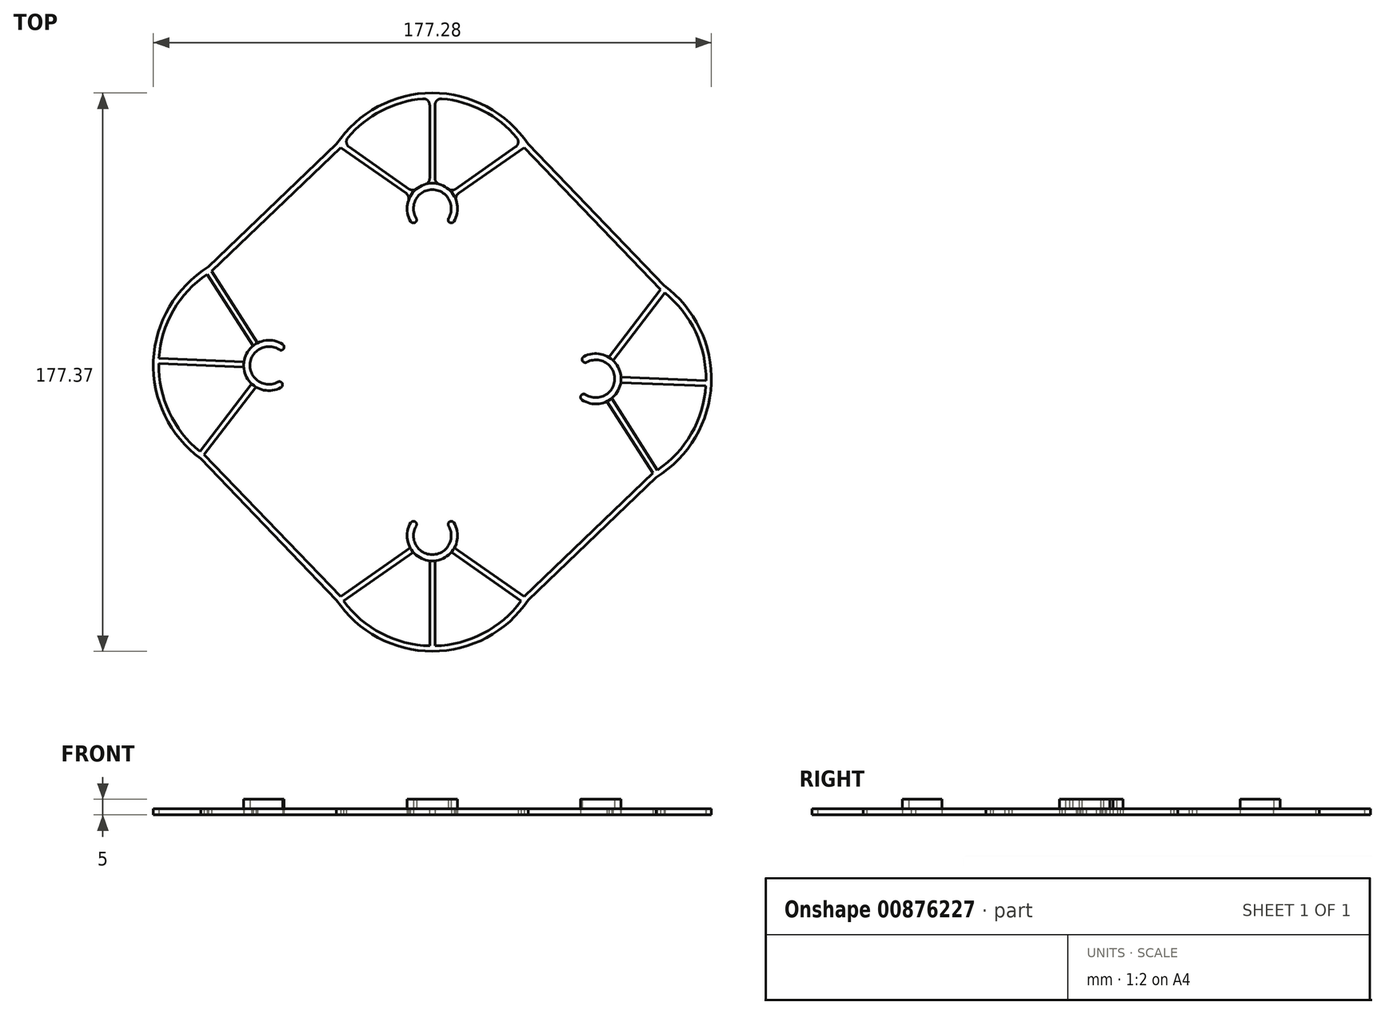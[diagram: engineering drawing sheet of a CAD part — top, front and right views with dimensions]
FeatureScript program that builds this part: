
annotation { "Feature Type Name" : "Feature", "Feature Type Description" : "" }
export const myFeature = defineFeature(function(context is Context, id is Id, definition is map)
    precondition{}
    {
        {
            var Q0;
            Q0=qCreatedBy(makeId("Top.planeOp"),FACE);
            var sketch = newSketch(context, id + "F0", { "sketchPlane" : qUnion([Q0])});
            skArc(sketch, "E0", {"start": v(5, -3.32) * mm, "mid": v(0, 6) * mm, "end": v(-5, -3.32) * mm});
            skArc(sketch, "E1", {"start": v(-7, 3.87) * mm, "mid": v(-7.85, -1.56) * mm, "end": v(-5, -6.24) * mm});
            skLineSegment(sketch, "E2", {"start": v(-7, 3.87) * mm, "end": v(-29.15, 19.37) * mm});
            skArc(sketch, "E3", {"start": v(28.17, 20.77) * mm, "mid": v(16.16, 31.05) * mm, "end": v(0.85, 34.99) * mm});
            skLineSegment(sketch, "E4", {"start": v(-6.03, 5.26) * mm, "end": v(-28.17, 20.77) * mm});
            skLineSegment(sketch, "E5", {"start": v(0, 0) * mm, "end": v(-28.67, 20.08) * mm, "construction": true});
            skLineSegment(sketch, "E6", {"start": v(0, 0) * mm, "end": v(0, 35) * mm, "construction": true});
            skLineSegment(sketch, "E7.MirrorCS", {"start": v(6.03, 5.26) * mm, "end": v(28.17, 20.77) * mm});
            skLineSegment(sketch, "E8.MirrorCS", {"start": v(7, 3.87) * mm, "end": v(29.15, 19.37) * mm});
            skLineSegment(sketch, "E9", {"start": v(-0.85, 7.95) * mm, "end": v(-0.85, 34.99) * mm});
            skLineSegment(sketch, "E10", {"start": v(0.85, 34.99) * mm, "end": v(0.85, 7.95) * mm});
            skArc(sketch, "E11", {"start": v(30.49, 20.43) * mm, "mid": v(0, 36.7) * mm, "end": v(-30.49, 20.43) * mm});
            skArc(sketch, "E12.trimOffspring", {"start": v(-0.85, 7.95) * mm, "mid": v(-3.7, 7.1) * mm, "end": v(-6.03, 5.26) * mm});
            skArc(sketch, "E13.trimOffspring", {"start": v(6.03, 5.26) * mm, "mid": v(3.7, 7.1) * mm, "end": v(0.85, 7.95) * mm});
            skArc(sketch, "E14.trimOffspring", {"start": v(-0.85, 34.99) * mm, "mid": v(-16.16, 31.05) * mm, "end": v(-28.17, 20.77) * mm});
            skPoint(sketch, "E15.middle", {"position": v(0, -9.2) * mm});
            skPoint(sketch, "E15.bottom.start.orphan", {"position": v(-4, -0.06) * mm});
            skPoint(sketch, "E16.orphan", {"position": v(4, 0.05) * mm});
            skArc(sketch, "E17.trimOffspring", {"start": v(5, -6.24) * mm, "mid": v(7.85, -1.56) * mm, "end": v(7, 3.87) * mm});
            skPoint(sketch, "E15.top.end.orphan", {"position": v(4, -18.32) * mm});
            skPoint(sketch, "E15.top.start.orphan", {"position": v(-4, -18.43) * mm});
            skLineSegment(sketch, "E18", {"start": v(0, 0) * mm, "end": v(51.94, -54.1) * mm, "construction": true});
            skLineSegment(sketch, "E19", {"start": v(51.94, -54.1) * mm, "end": v(0, -103.97) * mm, "construction": true});
            skLineSegment(sketch, "E20", {"start": v(0, -103.97) * mm, "end": v(-51.94, -49.86) * mm, "construction": true});
            skLineSegment(sketch, "E21", {"start": v(-51.94, -49.86) * mm, "end": v(0, 0) * mm, "construction": true});
            skLineSegment(sketch, "E22", {"start": v(0, 0) * mm, "end": v(0, -103.97) * mm, "construction": true});
            skLineSegment(sketch, "E23", {"start": v(51.94, -54.1) * mm, "end": v(-51.94, -49.86) * mm, "construction": true});
            skLineSegment(sketch, "E24", {"start": v(0, -51.98) * mm, "end": v(54.15, 0) * mm, "construction": true});
            skLineSegment(sketch, "E25.MirrorCS", {"start": v(48.42, -58.96) * mm, "end": v(45.5, -58.85) * mm});
            skLineSegment(sketch, "E26.MirrorCS", {"start": v(48.83, -48.97) * mm, "end": v(45.9, -48.85) * mm});
            skArc(sketch, "E27.MirrorCS", {"start": v(57.44, -48.3) * mm, "mid": v(59.18, -50.7) * mm, "end": v(59.92, -53.58) * mm});
            skArc(sketch, "E28.MirrorCS", {"start": v(59.85, -55.28) * mm, "mid": v(58.88, -58.08) * mm, "end": v(56.95, -60.34) * mm});
            skLineSegment(sketch, "E29.MirrorCS", {"start": v(55.52, -61.26) * mm, "end": v(70.1, -84.02) * mm});
            skLineSegment(sketch, "E30.MirrorCS", {"start": v(57.44, -48.3) * mm, "end": v(73.84, -26.8) * mm});
            skArc(sketch, "E31.MirrorCS", {"start": v(55.52, -61.26) * mm, "mid": v(50.07, -61.88) * mm, "end": v(45.5, -58.85) * mm});
            skPoint(sketch, "E32.MirrorP", {"position": v(51.71, -58.1) * mm});
            skLineSegment(sketch, "E33.MirrorCS", {"start": v(56.09, -47.26) * mm, "end": v(72.49, -25.77) * mm});
            skLineSegment(sketch, "E34.MirrorCS", {"start": v(56.95, -60.34) * mm, "end": v(71.54, -83.1) * mm});
            skArc(sketch, "E35.MirrorCS", {"start": v(73.6, -24.47) * mm, "mid": v(88.6, -55.6) * mm, "end": v(71.1, -85.4) * mm});
            skArc(sketch, "E36.MirrorCS", {"start": v(73.84, -26.8) * mm, "mid": v(83.62, -39.22) * mm, "end": v(86.94, -54.68) * mm});
            skLineSegment(sketch, "E37.MirrorCS", {"start": v(59.85, -55.28) * mm, "end": v(86.87, -56.38) * mm});
            skLineSegment(sketch, "E38.MirrorCS", {"start": v(86.94, -54.68) * mm, "end": v(59.92, -53.58) * mm});
            skArc(sketch, "E39.MirrorCS", {"start": v(48.83, -48.97) * mm, "mid": v(57.93, -54.35) * mm, "end": v(48.42, -58.96) * mm});
            skPoint(sketch, "E40.MirrorP", {"position": v(52.15, -50.1) * mm});
            skArc(sketch, "E41.MirrorCS", {"start": v(45.9, -48.85) * mm, "mid": v(50.7, -46.2) * mm, "end": v(56.09, -47.26) * mm});
            skArc(sketch, "E42.MirrorCS", {"start": v(86.87, -56.38) * mm, "mid": v(82.3, -71.52) * mm, "end": v(71.54, -83.1) * mm});
            skLineSegment(sketch, "E43", {"start": v(0, -51.98) * mm, "end": v(-83.37, 34.86) * mm, "construction": true});
            skArc(sketch, "E44.MirrorCS", {"start": v(-45.9, -55.11) * mm, "mid": v(-50.7, -57.77) * mm, "end": v(-56.09, -56.7) * mm});
            skLineSegment(sketch, "E45.MirrorCS", {"start": v(-48.83, -55) * mm, "end": v(-45.9, -55.11) * mm});
            skArc(sketch, "E46.MirrorCS", {"start": v(-57.44, -55.67) * mm, "mid": v(-59.18, -53.26) * mm, "end": v(-59.92, -50.39) * mm});
            skLineSegment(sketch, "E47.MirrorCS", {"start": v(-48.42, -45) * mm, "end": v(-45.5, -45.12) * mm});
            skArc(sketch, "E48.MirrorCS", {"start": v(-73.6, -79.5) * mm, "mid": v(-88.6, -48.36) * mm, "end": v(-71.1, -18.57) * mm});
            skArc(sketch, "E49.MirrorCS", {"start": v(-59.85, -48.69) * mm, "mid": v(-58.88, -45.88) * mm, "end": v(-56.95, -43.62) * mm});
            skArc(sketch, "E50.MirrorCS", {"start": v(-73.84, -77.17) * mm, "mid": v(-83.62, -64.74) * mm, "end": v(-86.94, -49.28) * mm});
            skPoint(sketch, "E51.MirrorP", {"position": v(-52.15, -53.86) * mm});
            skArc(sketch, "E52.MirrorCS", {"start": v(-86.87, -47.59) * mm, "mid": v(-82.3, -32.45) * mm, "end": v(-71.54, -20.86) * mm});
            skLineSegment(sketch, "E53.MirrorCS", {"start": v(-59.85, -48.69) * mm, "end": v(-86.87, -47.59) * mm});
            skPoint(sketch, "E54.MirrorP", {"position": v(-42.76, -50.24) * mm});
            skArc(sketch, "E55.MirrorCS", {"start": v(-48.83, -55) * mm, "mid": v(-57.93, -49.62) * mm, "end": v(-48.42, -45) * mm});
            skLineSegment(sketch, "E56.MirrorCS", {"start": v(-56.95, -43.62) * mm, "end": v(-71.54, -20.86) * mm});
            skArc(sketch, "E57.MirrorCS", {"start": v(-55.52, -42.7) * mm, "mid": v(-50.07, -42.08) * mm, "end": v(-45.5, -45.12) * mm});
            skLineSegment(sketch, "E58.MirrorCS", {"start": v(-56.09, -56.7) * mm, "end": v(-72.49, -78.2) * mm});
            skLineSegment(sketch, "E59.MirrorCS", {"start": v(-55.52, -42.7) * mm, "end": v(-70.1, -19.95) * mm});
            skPoint(sketch, "E60.MirrorP", {"position": v(-51.71, -45.87) * mm});
            skLineSegment(sketch, "E61.MirrorCS", {"start": v(-57.44, -55.67) * mm, "end": v(-73.84, -77.17) * mm});
            skLineSegment(sketch, "E62.MirrorCS", {"start": v(-86.94, -49.28) * mm, "end": v(-59.92, -50.39) * mm});
            skLineSegment(sketch, "E63.MirrorCS", {"start": v(-5, -100.65) * mm, "end": v(-5, -97.72) * mm});
            skArc(sketch, "E64.MirrorCS", {"start": v(0.85, -111.92) * mm, "mid": v(3.7, -111.06) * mm, "end": v(6.03, -109.23) * mm});
            skArc(sketch, "E65.MirrorCS", {"start": v(-6.03, -109.23) * mm, "mid": v(-3.7, -111.06) * mm, "end": v(-0.85, -111.92) * mm});
            skLineSegment(sketch, "E66.MirrorCS", {"start": v(5, -100.65) * mm, "end": v(5, -97.72) * mm});
            skLineSegment(sketch, "E67.MirrorCS", {"start": v(-6.03, -109.23) * mm, "end": v(-28.17, -124.73) * mm});
            skArc(sketch, "E68.MirrorCS", {"start": v(-30.49, -124.4) * mm, "mid": v(0, -140.67) * mm, "end": v(30.49, -124.4) * mm});
            skArc(sketch, "E69.MirrorCS", {"start": v(-5, -97.72) * mm, "mid": v(-7.85, -102.41) * mm, "end": v(-7, -107.83) * mm});
            skArc(sketch, "E70.MirrorCS", {"start": v(-5, -100.65) * mm, "mid": v(0, -109.97) * mm, "end": v(5, -100.65) * mm});
            skArc(sketch, "E71.MirrorCS", {"start": v(-28.17, -124.73) * mm, "mid": v(-16.16, -135.01) * mm, "end": v(-0.85, -138.96) * mm});
            skPoint(sketch, "E72.MirrorP", {"position": v(-4, -104.01) * mm});
            skLineSegment(sketch, "E73.MirrorCS", {"start": v(-7, -107.83) * mm, "end": v(-29.15, -123.34) * mm});
            skLineSegment(sketch, "E74.MirrorCS", {"start": v(0.85, -111.92) * mm, "end": v(0.85, -138.96) * mm});
            skArc(sketch, "E75.MirrorCS", {"start": v(7, -107.83) * mm, "mid": v(7.85, -102.41) * mm, "end": v(5, -97.72) * mm});
            skPoint(sketch, "E76.MirrorP", {"position": v(4, -103.9) * mm});
            skLineSegment(sketch, "E77.MirrorCS", {"start": v(-0.85, -138.96) * mm, "end": v(-0.85, -111.92) * mm});
            skLineSegment(sketch, "E78.MirrorCS", {"start": v(7, -107.83) * mm, "end": v(29.15, -123.34) * mm});
            skLineSegment(sketch, "E79.MirrorCS", {"start": v(6.03, -109.23) * mm, "end": v(28.17, -124.73) * mm});
            skArc(sketch, "E80.MirrorCS", {"start": v(0.85, -138.96) * mm, "mid": v(16.16, -135.01) * mm, "end": v(28.17, -124.73) * mm});
            skLineSegment(sketch, "E81", {"start": v(73.6, -24.47) * mm, "end": v(30.49, 20.43) * mm});
            skLineSegment(sketch, "E82", {"start": v(72.49, -25.77) * mm, "end": v(29.15, 19.37) * mm});
            skLineSegment(sketch, "E83", {"start": v(71.1, -85.4) * mm, "end": v(30.49, -124.4) * mm});
            skLineSegment(sketch, "E84", {"start": v(70.1, -84.02) * mm, "end": v(29.15, -123.34) * mm});
            skLineSegment(sketch, "E85", {"start": v(-30.49, -124.4) * mm, "end": v(-73.6, -79.5) * mm});
            skLineSegment(sketch, "E86", {"start": v(-29.15, -123.34) * mm, "end": v(-72.49, -78.2) * mm});
            skLineSegment(sketch, "E87", {"start": v(-71.1, -18.57) * mm, "end": v(-30.49, 20.43) * mm});
            skLineSegment(sketch, "E88", {"start": v(-29.15, 19.37) * mm, "end": v(-70.1, -19.95) * mm});
            skLineSegment(sketch, "E89", {"start": v(-5, -3.32) * mm, "end": v(-5, -6.24) * mm});
            skLineSegment(sketch, "E90", {"start": v(5, -3.32) * mm, "end": v(5, -6.24) * mm});
            skSolve(sketch);
        }
        {
            var Q0;
            Q0=qSketchRegion(id+"F0",true);
            extrude(context, id + "F1", {"entities" : qUnion([Q0]), "depth" : 2 * mm});
        }
        {
            var Q0;
            Q0=makeQuery(id+"F1.opExtrude","SWEPT_EDGE",EDGE,{"disambiguationData":[OSD([sQuery(id+"F0.wireOp",EDGE,"E0"),sQuery(id+"F0.wireOp",EDGE,"E89")])]});
            var Q1;
            Q1=makeQuery(id+"F1.opExtrude","SWEPT_EDGE",EDGE,{"disambiguationData":[OSD([sQuery(id+"F0.wireOp",EDGE,"E1"),sQuery(id+"F0.wireOp",EDGE,"E89")])]});
            var Q2;
            Q2=makeQuery(id+"F1.opExtrude","SWEPT_EDGE",EDGE,{"disambiguationData":[OSD([sQuery(id+"F0.wireOp",EDGE,"E0"),sQuery(id+"F0.wireOp",EDGE,"E90")])]});
            var Q3;
            Q3=makeQuery(id+"F1.opExtrude","SWEPT_EDGE",EDGE,{"disambiguationData":[OSD([sQuery(id+"F0.wireOp",EDGE,"E17.trimOffspring"),sQuery(id+"F0.wireOp",EDGE,"E90")])]});
            var Q4;
            Q4=makeQuery(id+"F1.opExtrude","SWEPT_EDGE",EDGE,{"disambiguationData":[OSD([sQuery(id+"F0.wireOp",EDGE,"E26.MirrorCS"),sQuery(id+"F0.wireOp",EDGE,"E39.MirrorCS")])]});
            var Q5;
            Q5=makeQuery(id+"F1.opExtrude","SWEPT_EDGE",EDGE,{"disambiguationData":[OSD([sQuery(id+"F0.wireOp",EDGE,"E26.MirrorCS"),sQuery(id+"F0.wireOp",EDGE,"E41.MirrorCS")])]});
            var Q6;
            Q6=makeQuery(id+"F1.opExtrude","SWEPT_EDGE",EDGE,{"disambiguationData":[OSD([sQuery(id+"F0.wireOp",EDGE,"E25.MirrorCS"),sQuery(id+"F0.wireOp",EDGE,"E39.MirrorCS")])]});
            var Q7;
            Q7=makeQuery(id+"F1.opExtrude","SWEPT_EDGE",EDGE,{"disambiguationData":[OSD([sQuery(id+"F0.wireOp",EDGE,"E25.MirrorCS"),sQuery(id+"F0.wireOp",EDGE,"E31.MirrorCS")])]});
            var Q8;
            Q8=makeQuery(id+"F1.opExtrude","SWEPT_EDGE",EDGE,{"disambiguationData":[OSD([sQuery(id+"F0.wireOp",EDGE,"E66.MirrorCS"),sQuery(id+"F0.wireOp",EDGE,"E70.MirrorCS")])]});
            var Q9;
            Q9=makeQuery(id+"F1.opExtrude","SWEPT_EDGE",EDGE,{"disambiguationData":[OSD([sQuery(id+"F0.wireOp",EDGE,"E66.MirrorCS"),sQuery(id+"F0.wireOp",EDGE,"E75.MirrorCS")])]});
            var Q10;
            Q10=makeQuery(id+"F1.opExtrude","SWEPT_EDGE",EDGE,{"disambiguationData":[OSD([sQuery(id+"F0.wireOp",EDGE,"E63.MirrorCS"),sQuery(id+"F0.wireOp",EDGE,"E69.MirrorCS")])]});
            var Q11;
            Q11=makeQuery(id+"F1.opExtrude","SWEPT_EDGE",EDGE,{"disambiguationData":[OSD([sQuery(id+"F0.wireOp",EDGE,"E63.MirrorCS"),sQuery(id+"F0.wireOp",EDGE,"E70.MirrorCS")])]});
            var Q12;
            Q12=makeQuery(id+"F1.opExtrude","SWEPT_EDGE",EDGE,{"disambiguationData":[OSD([sQuery(id+"F0.wireOp",EDGE,"E45.MirrorCS"),sQuery(id+"F0.wireOp",EDGE,"E55.MirrorCS")])]});
            var Q13;
            Q13=makeQuery(id+"F1.opExtrude","SWEPT_EDGE",EDGE,{"disambiguationData":[OSD([sQuery(id+"F0.wireOp",EDGE,"E44.MirrorCS"),sQuery(id+"F0.wireOp",EDGE,"E45.MirrorCS")])]});
            var Q14;
            Q14=makeQuery(id+"F1.opExtrude","SWEPT_EDGE",EDGE,{"disambiguationData":[OSD([sQuery(id+"F0.wireOp",EDGE,"E47.MirrorCS"),sQuery(id+"F0.wireOp",EDGE,"E55.MirrorCS")])]});
            var Q15;
            Q15=makeQuery(id+"F1.opExtrude","SWEPT_EDGE",EDGE,{"disambiguationData":[OSD([sQuery(id+"F0.wireOp",EDGE,"E47.MirrorCS"),sQuery(id+"F0.wireOp",EDGE,"E57.MirrorCS")])]});
            fillet(context, id + "F2", {"entities" : qUnion([Q0, Q1, Q2, Q3, Q4, Q5, Q6, Q7, Q8, Q9, Q10, Q11, Q12, Q13, Q14, Q15]), "radius" : 1 * mm, "tangentPropagation" : true, "allowEdgeOverflow" : false});
        }
        {
            var Q0;
            Q0=makeQuery(id+"F1.opExtrude","SWEPT_EDGE",EDGE,{"disambiguationData":[OSD([sQuery(id+"F0.wireOp",EDGE,"E7.MirrorCS"),sQuery(id+"F0.wireOp",EDGE,"E13.trimOffspring")])]});
            var Q1;
            Q1=makeQuery(id+"F1.opExtrude","SWEPT_EDGE",EDGE,{"disambiguationData":[OSD([sQuery(id+"F0.wireOp",EDGE,"E10"),sQuery(id+"F0.wireOp",EDGE,"E13.trimOffspring")])]});
            var Q2;
            Q2=makeQuery(id+"F1.opExtrude","SWEPT_EDGE",EDGE,{"disambiguationData":[OSD([sQuery(id+"F0.wireOp",EDGE,"E8.MirrorCS"),sQuery(id+"F0.wireOp",EDGE,"E17.trimOffspring")])]});
            var Q3;
            Q3=makeQuery(id+"F1.opExtrude","SWEPT_EDGE",EDGE,{"disambiguationData":[OSD([sQuery(id+"F0.wireOp",EDGE,"E9"),sQuery(id+"F0.wireOp",EDGE,"E12.trimOffspring")])]});
            var Q4;
            Q4=makeQuery(id+"F1.opExtrude","SWEPT_EDGE",EDGE,{"disambiguationData":[OSD([sQuery(id+"F0.wireOp",EDGE,"E1"),sQuery(id+"F0.wireOp",EDGE,"E2")])]});
            var Q5;
            Q5=makeQuery(id+"F1.opExtrude","SWEPT_EDGE",EDGE,{"disambiguationData":[OSD([sQuery(id+"F0.wireOp",EDGE,"E4"),sQuery(id+"F0.wireOp",EDGE,"E12.trimOffspring")])]});
            var Q6;
            Q6=makeQuery(id+"F1.opExtrude","SWEPT_EDGE",EDGE,{"disambiguationData":[OSD([sQuery(id+"F0.wireOp",EDGE,"E3"),sQuery(id+"F0.wireOp",EDGE,"E7.MirrorCS")])]});
            var Q7;
            Q7=makeQuery(id+"F1.opExtrude","SWEPT_EDGE",EDGE,{"disambiguationData":[OSD([sQuery(id+"F0.wireOp",EDGE,"E4"),sQuery(id+"F0.wireOp",EDGE,"E14.trimOffspring")])]});
            var Q8;
            Q8=makeQuery(id+"F1.opExtrude","SWEPT_EDGE",EDGE,{"disambiguationData":[OSD([sQuery(id+"F0.wireOp",EDGE,"E9"),sQuery(id+"F0.wireOp",EDGE,"E14.trimOffspring")])]});
            var Q9;
            Q9=makeQuery(id+"F1.opExtrude","SWEPT_EDGE",EDGE,{"disambiguationData":[OSD([sQuery(id+"F0.wireOp",EDGE,"E3"),sQuery(id+"F0.wireOp",EDGE,"E10")])]});
            fillet(context, id + "F3", {"entities" : qUnion([Q0, Q1, Q2, Q3, Q4, Q5, Q6, Q7, Q8, Q9]), "radius" : 2 * mm, "tangentPropagation" : true, "allowEdgeOverflow" : false});
        }
        {
            var Q0;
            Q0=makeQuery(id+"F1.opExtrude","CAP_FACE",FACE,{"disambiguationData":[OSD([sQuery(id+"F0.wireOp",EDGE,"E0"),sQuery(id+"F0.wireOp",EDGE,"E1"),sQuery(id+"F0.wireOp",EDGE,"E2"),sQuery(id+"F0.wireOp",EDGE,"E3"),sQuery(id+"F0.wireOp",EDGE,"E4"),sQuery(id+"F0.wireOp",EDGE,"E7.MirrorCS"),sQuery(id+"F0.wireOp",EDGE,"E8.MirrorCS"),sQuery(id+"F0.wireOp",EDGE,"E9"),sQuery(id+"F0.wireOp",EDGE,"E10"),sQuery(id+"F0.wireOp",EDGE,"E11"),sQuery(id+"F0.wireOp",EDGE,"E12.trimOffspring"),sQuery(id+"F0.wireOp",EDGE,"E13.trimOffspring"),sQuery(id+"F0.wireOp",EDGE,"E14.trimOffspring"),sQuery(id+"F0.wireOp",EDGE,"E15.left"),sQuery(id+"F0.wireOp",EDGE,"E15.right"),sQuery(id+"F0.wireOp",EDGE,"E17.trimOffspring"),sQuery(id+"F0.wireOp",EDGE,"E25.MirrorCS"),sQuery(id+"F0.wireOp",EDGE,"E26.MirrorCS"),sQuery(id+"F0.wireOp",EDGE,"E27.MirrorCS"),sQuery(id+"F0.wireOp",EDGE,"E28.MirrorCS"),sQuery(id+"F0.wireOp",EDGE,"E29.MirrorCS"),sQuery(id+"F0.wireOp",EDGE,"E30.MirrorCS"),sQuery(id+"F0.wireOp",EDGE,"E31.MirrorCS"),sQuery(id+"F0.wireOp",EDGE,"E33.MirrorCS"),sQuery(id+"F0.wireOp",EDGE,"E34.MirrorCS"),sQuery(id+"F0.wireOp",EDGE,"E35.MirrorCS"),sQuery(id+"F0.wireOp",EDGE,"E36.MirrorCS"),sQuery(id+"F0.wireOp",EDGE,"E37.MirrorCS"),sQuery(id+"F0.wireOp",EDGE,"E38.MirrorCS"),sQuery(id+"F0.wireOp",EDGE,"E39.MirrorCS"),sQuery(id+"F0.wireOp",EDGE,"E41.MirrorCS"),sQuery(id+"F0.wireOp",EDGE,"E42.MirrorCS"),sQuery(id+"F0.wireOp",EDGE,"E44.MirrorCS"),sQuery(id+"F0.wireOp",EDGE,"E45.MirrorCS"),sQuery(id+"F0.wireOp",EDGE,"E46.MirrorCS"),sQuery(id+"F0.wireOp",EDGE,"E47.MirrorCS"),sQuery(id+"F0.wireOp",EDGE,"E48.MirrorCS"),sQuery(id+"F0.wireOp",EDGE,"E49.MirrorCS"),sQuery(id+"F0.wireOp",EDGE,"E50.MirrorCS"),sQuery(id+"F0.wireOp",EDGE,"E52.MirrorCS"),sQuery(id+"F0.wireOp",EDGE,"E53.MirrorCS"),sQuery(id+"F0.wireOp",EDGE,"E55.MirrorCS"),sQuery(id+"F0.wireOp",EDGE,"E56.MirrorCS"),sQuery(id+"F0.wireOp",EDGE,"E57.MirrorCS"),sQuery(id+"F0.wireOp",EDGE,"E58.MirrorCS"),sQuery(id+"F0.wireOp",EDGE,"E59.MirrorCS"),sQuery(id+"F0.wireOp",EDGE,"E61.MirrorCS"),sQuery(id+"F0.wireOp",EDGE,"E62.MirrorCS"),sQuery(id+"F0.wireOp",EDGE,"E63.MirrorCS"),sQuery(id+"F0.wireOp",EDGE,"E64.MirrorCS"),sQuery(id+"F0.wireOp",EDGE,"E65.MirrorCS"),sQuery(id+"F0.wireOp",EDGE,"E66.MirrorCS"),sQuery(id+"F0.wireOp",EDGE,"E67.MirrorCS"),sQuery(id+"F0.wireOp",EDGE,"E68.MirrorCS"),sQuery(id+"F0.wireOp",EDGE,"E69.MirrorCS"),sQuery(id+"F0.wireOp",EDGE,"E70.MirrorCS"),sQuery(id+"F0.wireOp",EDGE,"E71.MirrorCS"),sQuery(id+"F0.wireOp",EDGE,"E73.MirrorCS"),sQuery(id+"F0.wireOp",EDGE,"E74.MirrorCS"),sQuery(id+"F0.wireOp",EDGE,"E75.MirrorCS"),sQuery(id+"F0.wireOp",EDGE,"E77.MirrorCS"),sQuery(id+"F0.wireOp",EDGE,"E78.MirrorCS"),sQuery(id+"F0.wireOp",EDGE,"E79.MirrorCS"),sQuery(id+"F0.wireOp",EDGE,"E80.MirrorCS"),sQuery(id+"F0.wireOp",EDGE,"E81"),sQuery(id+"F0.wireOp",EDGE,"E82"),sQuery(id+"F0.wireOp",EDGE,"E83"),sQuery(id+"F0.wireOp",EDGE,"E84"),sQuery(id+"F0.wireOp",EDGE,"E85"),sQuery(id+"F0.wireOp",EDGE,"E86"),sQuery(id+"F0.wireOp",EDGE,"E87"),sQuery(id+"F0.wireOp",EDGE,"E88")])],"isStart":false});
            var sketch = newSketch(context, id + "F4", { "sketchPlane" : qUnion([Q0])});
            skLineSegment(sketch, "E91.0", {"start": v(73.6, -24.47) * mm, "end": v(30.49, 20.43) * mm});
            skArc(sketch, "E92.0", {"start": v(73.6, -24.47) * mm, "mid": v(88.6, -55.6) * mm, "end": v(71.1, -85.4) * mm});
            skLineSegment(sketch, "E93.0", {"start": v(71.1, -85.4) * mm, "end": v(30.49, -124.4) * mm});
            skArc(sketch, "E94.0", {"start": v(-30.49, -124.4) * mm, "mid": v(0, -140.67) * mm, "end": v(30.49, -124.4) * mm});
            skLineSegment(sketch, "E95.0", {"start": v(-30.49, -124.4) * mm, "end": v(-73.6, -79.5) * mm});
            skArc(sketch, "E96.0", {"start": v(-73.6, -79.5) * mm, "mid": v(-88.6, -48.36) * mm, "end": v(-71.1, -18.57) * mm});
            skLineSegment(sketch, "E97.0", {"start": v(-71.1, -18.57) * mm, "end": v(-30.49, 20.43) * mm});
            skArc(sketch, "E98.0", {"start": v(30.49, 20.43) * mm, "mid": v(0, 36.7) * mm, "end": v(-30.49, 20.43) * mm});
            skArc(sketch, "E99.0", {"start": v(72.7, -25.5) * mm, "mid": v(87.26, -55.56) * mm, "end": v(70.28, -84.33) * mm});
            skLineSegment(sketch, "E99.1", {"start": v(70.28, -84.33) * mm, "end": v(29.45, -123.52) * mm});
            skLineSegment(sketch, "E99.2", {"start": v(72.7, -25.5) * mm, "end": v(29.43, 19.58) * mm});
            skArc(sketch, "E99.3", {"start": v(-29.43, -123.55) * mm, "mid": v(0.01, -139.32) * mm, "end": v(29.45, -123.52) * mm});
            skArc(sketch, "E99.4", {"start": v(29.43, 19.58) * mm, "mid": v(-0.01, 35.35) * mm, "end": v(-29.45, 19.56) * mm});
            skLineSegment(sketch, "E99.5", {"start": v(-70.28, -19.64) * mm, "end": v(-29.45, 19.56) * mm});
            skArc(sketch, "E99.6", {"start": v(-72.7, -78.47) * mm, "mid": v(-87.26, -48.4) * mm, "end": v(-70.28, -19.64) * mm});
            skLineSegment(sketch, "E99.7", {"start": v(-29.43, -123.55) * mm, "end": v(-72.7, -78.47) * mm});
            skSolve(sketch);
        }
        {
            var Q0;
            Q0=makeQuery(id+"F4.imprint","IMPRINT",FACE,{"disambiguationData":[TD([[makeQuery(id+"F4.imprint","IMPRINT",EDGE,{"derivedFrom":sQuery(id+"F4.wireOp",EDGE,"E99.0")}),-1.0]])]});
            var sketch = newSketch(context, id + "F5", { "sketchPlane" : qUnion([Q0])});
            skArc(sketch, "E100.0", {"start": v(-49.06, -55.13) * mm, "mid": v(-57.93, -49.62) * mm, "end": v(-48.64, -44.85) * mm, "construction": true});
            skArc(sketch, "E101.0", {"start": v(-48.64, -44.85) * mm, "mid": v(-47.26, -44.56) * mm, "end": v(-47.54, -43.18) * mm});
            skPoint(sketch, "E102.0", {"position": v(-48.1, -56.88) * mm});
            skArc(sketch, "E103.0", {"start": v(-48.1, -56.88) * mm, "mid": v(-47.7, -55.52) * mm, "end": v(-49.06, -55.13) * mm});
            skArc(sketch, "E104.0", {"start": v(-5.14, -100.88) * mm, "mid": v(0, -109.97) * mm, "end": v(5.14, -100.88) * mm, "construction": true});
            skArc(sketch, "E105.0", {"start": v(6.86, -99.85) * mm, "mid": v(5.48, -99.5) * mm, "end": v(5.14, -100.88) * mm});
            skArc(sketch, "E106.0", {"start": v(-5.14, -100.88) * mm, "mid": v(-5.48, -99.5) * mm, "end": v(-6.86, -99.85) * mm});
            skArc(sketch, "E107.0", {"start": v(49.06, -48.84) * mm, "mid": v(57.93, -54.35) * mm, "end": v(48.64, -59.12) * mm, "construction": true});
            skArc(sketch, "E108.0", {"start": v(48.64, -59.12) * mm, "mid": v(47.26, -59.4) * mm, "end": v(47.54, -60.79) * mm});
            skArc(sketch, "E109.0", {"start": v(48.1, -47.08) * mm, "mid": v(47.7, -48.44) * mm, "end": v(49.06, -48.84) * mm});
            skArc(sketch, "E110.0", {"start": v(5.14, -3.1) * mm, "mid": v(0, 6) * mm, "end": v(-5.14, -3.1) * mm, "construction": true});
            skArc(sketch, "E111.0", {"start": v(5.14, -3.1) * mm, "mid": v(5.48, -4.46) * mm, "end": v(6.86, -4.12) * mm});
            skArc(sketch, "E112.0", {"start": v(-6.86, -4.12) * mm, "mid": v(-5.48, -4.46) * mm, "end": v(-5.14, -3.1) * mm});
            skArc(sketch, "E113", {"start": v(5.14, -3.1) * mm, "mid": v(0, 6) * mm, "end": v(-5.14, -3.1) * mm});
            skArc(sketch, "E114", {"start": v(6.86, -4.12) * mm, "mid": v(0, 8) * mm, "end": v(-6.86, -4.12) * mm});
            skArc(sketch, "E115", {"start": v(48.64, -59.12) * mm, "mid": v(57.93, -54.35) * mm, "end": v(49.06, -48.84) * mm});
            skArc(sketch, "E116", {"start": v(47.54, -60.79) * mm, "mid": v(59.93, -54.43) * mm, "end": v(48.1, -47.08) * mm});
            skArc(sketch, "E117", {"start": v(-5.14, -100.88) * mm, "mid": v(0, -109.97) * mm, "end": v(5.14, -100.88) * mm});
            skArc(sketch, "E118", {"start": v(-6.86, -99.85) * mm, "mid": v(0, -111.97) * mm, "end": v(6.86, -99.85) * mm});
            skArc(sketch, "E119", {"start": v(-48.64, -44.85) * mm, "mid": v(-57.93, -49.62) * mm, "end": v(-49.06, -55.13) * mm});
            skArc(sketch, "E120", {"start": v(-47.54, -43.18) * mm, "mid": v(-59.93, -49.54) * mm, "end": v(-48.1, -56.88) * mm});
            skSolve(sketch);
        }
        {
            var Q0;
            Q0=qSketchRegion(id+"F5",true);
            extrude(context, id + "F6", {"entities" : qUnion([Q0]), "operationType" : NewBodyOperationType.ADD, "depth" : 3 * mm});
        }
    });
